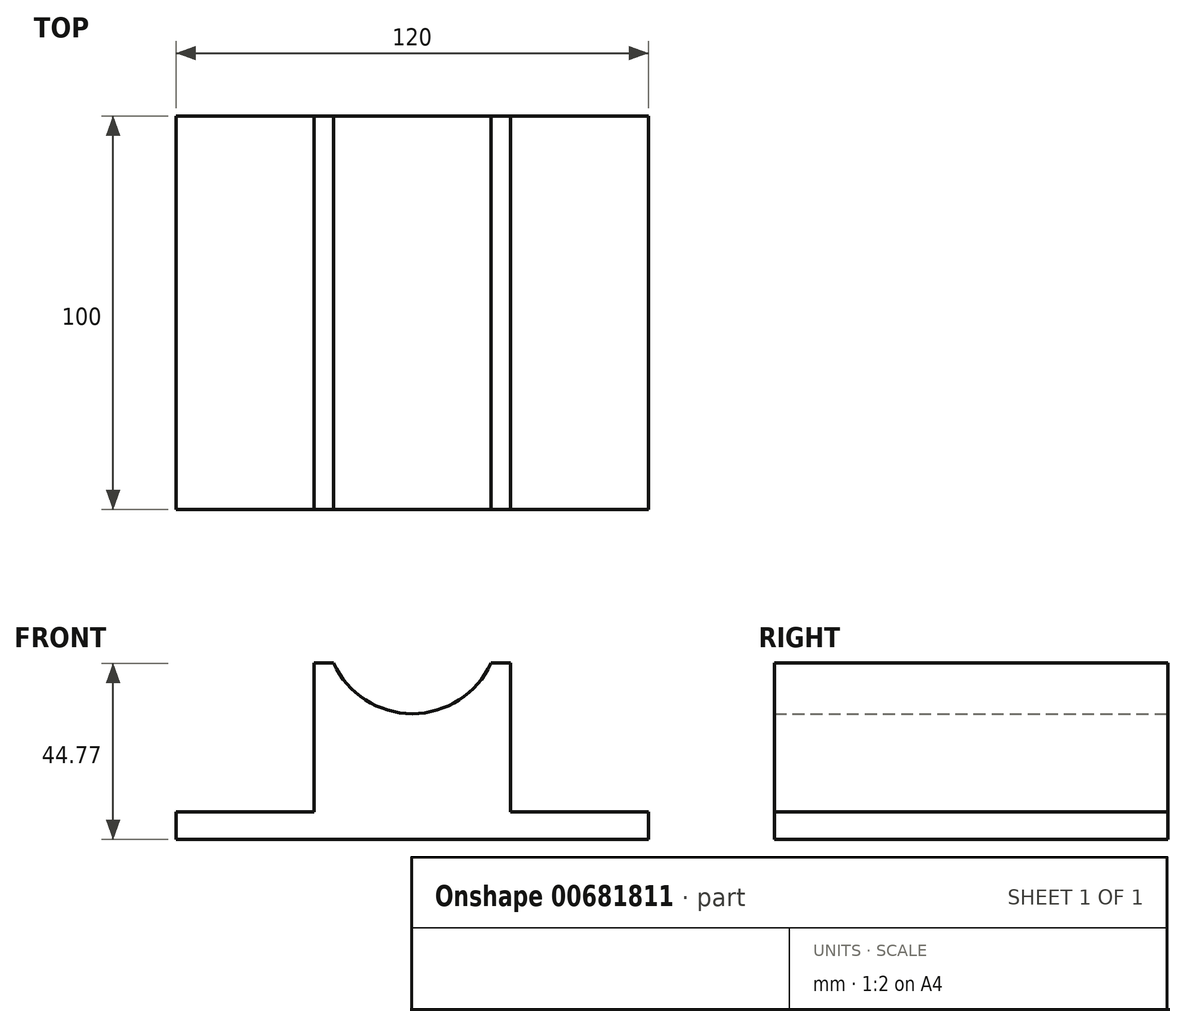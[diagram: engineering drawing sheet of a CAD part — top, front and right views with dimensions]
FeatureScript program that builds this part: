
annotation { "Feature Type Name" : "Feature", "Feature Type Description" : "" }
export const myFeature = defineFeature(function(context is Context, id is Id, definition is map)
    precondition{}
    {
        {
            var Q0;
            Q0=qCreatedBy(makeId("Front.planeOp"),FACE);
            var sketch = newSketch(context, id + "F0", { "sketchPlane" : qUnion([Q0])});
            skLineSegment(sketch, "E0.bottom", {"start": v(-73.33, -17.52) * mm, "end": v(46.67, -17.52) * mm});
            skLineSegment(sketch, "E0.top", {"start": v(-73.33, -24.52) * mm, "end": v(46.67, -24.52) * mm});
            skLineSegment(sketch, "E0.left", {"start": v(-73.33, -17.52) * mm, "end": v(-73.33, -24.52) * mm});
            skLineSegment(sketch, "E0.right", {"start": v(46.67, -17.52) * mm, "end": v(46.67, -24.52) * mm});
            skLineSegment(sketch, "E1", {"start": v(-13.33, -17.52) * mm, "end": v(-13.33, 20.25) * mm});
            skLineSegment(sketch, "E2.bottom", {"start": v(-38.33, -17.52) * mm, "end": v(11.67, -17.52) * mm});
            skLineSegment(sketch, "E2.top", {"start": v(-38.33, 20.25) * mm, "end": v(11.67, 20.25) * mm});
            skLineSegment(sketch, "E2.left", {"start": v(-38.33, -17.52) * mm, "end": v(-38.33, 20.25) * mm});
            skLineSegment(sketch, "E2.right", {"start": v(11.67, -17.52) * mm, "end": v(11.67, 20.25) * mm});
            skPoint(sketch, "E3", {"position": v(-33.33, 20.25) * mm});
            skPoint(sketch, "E4", {"position": v(6.67, 20.25) * mm});
            skArc(sketch, "E5", {"start": v(-33.33, 20.25) * mm, "mid": v(-13.33, 7.42) * mm, "end": v(6.67, 20.25) * mm});
            skSolve(sketch);
        }
        {
            var Q0;
            {var subQ0=sQuery(id+"F0.wireOp",EDGE,"E2.left");Q0=makeQuery(id+"F0.imprint","IMPRINT",FACE,{"disambiguationData":[TD([[makeQuery(id+"F0.imprint","IMPRINT",EDGE,{"derivedFrom":subQ0}),-1.0]])]});}
            var Q1;
            {var subQ0=sQuery(id+"F0.wireOp",EDGE,"E2.right");Q1=makeQuery(id+"F0.imprint","IMPRINT",FACE,{"disambiguationData":[TD([[makeQuery(id+"F0.imprint","IMPRINT",EDGE,{"derivedFrom":subQ0}),1.0]])]});}
            var Q2;
            Q2=makeQuery(id+"F0.imprint","IMPRINT",FACE,{"disambiguationData":[TD([[makeQuery(id+"F0.imprint","IMPRINT",EDGE,{"derivedFrom":sQuery(id+"F0.wireOp",EDGE,"E0.top")}),1.0]])]});
            extrude(context, id + "F1", {"entities" : qUnion([Q0, Q1, Q2]), "depth" : 100 * mm, "offsetDistance" : 25 * mm});
        }
    });
